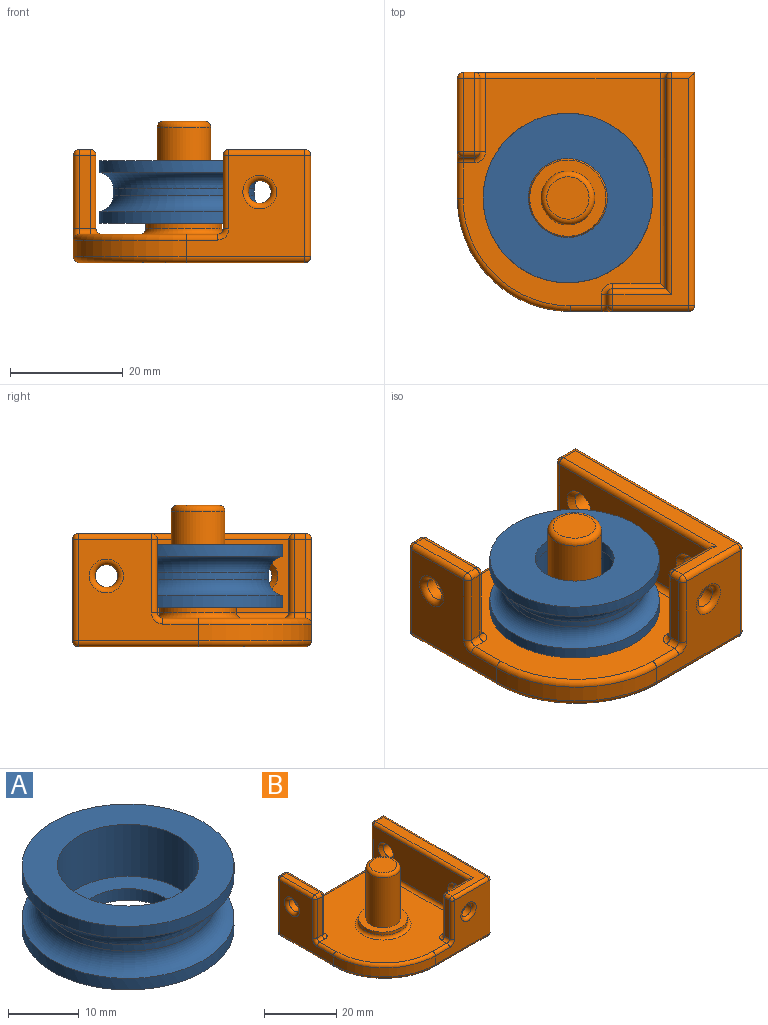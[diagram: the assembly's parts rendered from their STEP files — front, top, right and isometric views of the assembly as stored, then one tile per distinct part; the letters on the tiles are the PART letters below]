
ASSEMBLY  parts=2 mates=1
PART A: 10 faces, bbox 33.6x33.6x11 mm
  f0: plane 20x20mm, normal (0,0,1), area 160.2mm2, adj f1,f4
  f1: cylinder r=7mm len=14mm, axis (0,0,-1), area 88mm2, adj f0,f3
  f2: cylinder r=15mm len=30mm, axis (0,0,-1), area 188.5mm2, adj f3,f8
  f3: plane 30x30mm, normal (0,0,-1), area 552.9mm2, adj f1,f2
  f4: cylinder r=10mm len=20mm, axis (0,0,-1), area 565.5mm2, adj f0,f7
  f5: cylinder r=12.5mm len=25mm, axis (0,0,-1), area 85.1mm2, adj f8,f9
  f6: cylinder r=15mm len=30mm, axis (0,0,-1), area 188.5mm2, adj f7,f9
  f7: plane 30x30mm, normal (0,0,1), area 392.7mm2, adj f4,f6
  f8: torus R=15.5mm, axis (0,0,-1), area 354.3mm2, adj f2,f5
  f9: torus R=15.5mm, axis (0,0,1), area 354.3mm2, adj f5,f6
PART B: 78 faces, bbox 43.6x44x25 mm
  f0: plane 40.3x34.91mm, normal (0,0,1), area 1041.1mm2, adj f35,f36,f43,f48,f49,f59,f60,f63
  f1: plane 41x18mm, normal (0,1,0), area 216.1mm2, adj f5,f24,f34,f42,f46,f47,f48,f53
  f2: plane 21.3x18mm, normal (-1,0,0), area 231.4mm2, adj f3,f45,f55,f65,f68,f70,f71,f73
  f3: cylinder r=20mm len=20mm, axis (0,0,-1), area 94.2mm2, adj f2,f4,f40,f64
  f4: plane 21x18mm, normal (0,-1,0), area 237.7mm2, adj f3,f28,f32,f39,f50,f54,f60,f74
  f5: plane 41.3x18mm, normal (1,0,0), area 718.3mm2, adj f1,f20,f21,f27,f28,f41
  f6: plane 40.3x40mm, normal (0,0,-1), area 1534.6mm2, adj f32,f40,f41,f45,f46
  f7: plane 37.3x13mm, normal (-1,0,0), area 428.4mm2, adj f8,f22,f23,f25,f34,f35
  f8: plane 13x9.38mm, normal (0,1,0), area 93.7mm2, adj f7,f26,f36,f37,f75
  f9: plane 13x2mm, normal (-1,0,0), area 26mm2, adj f37,f38,f49,f50
  f10: plane 40.3x13.47mm, normal (0,0,1), area 145.3mm2, adj f24,f25,f26,f27,f38,f39
  f11: plane 13x12.99mm, normal (1,0,0), area 140.6mm2, adj f47,f57,f58,f59,f72
  f12: plane 13x2mm, normal (0,-1,0), area 26mm2, adj f58,f66,f67,f71
  f13: plane 12.99x2mm, normal (0,0,1), area 26mm2, adj f56,f57,f65,f66
  f14: cylinder r=6.75mm len=13.5mm, axis (0,0,-1), area 42.4mm2, adj f15,f77
  f15: plane 13.5x13.5mm, normal (0,0,1), area 72.3mm2, adj f14,f16
  f16: cylinder r=4.75mm len=17mm, axis (0,0,-1), area 507.4mm2, adj f15,f76
  f17: plane 7.5x7.5mm, normal (0,0,1), area 44.2mm2, adj f76
  f18: cylinder r=2mm len=4mm, axis (0,-1,0), area 25.1mm2, adj f74,f75
  f19: cylinder r=2mm len=4mm, axis (-1,0,0), area 25.1mm2, adj f72,f73
  f20: cylinder r=2mm len=4.09mm, axis (-1,0,0), area 51.4mm2, adj f5,f23
  f21: cylinder r=2mm len=4.09mm, axis (-1,0,0), area 51.4mm2, adj f5,f22
  f22: cone r=2mm half-angle=45deg, axis (-1,0,0), area 22.2mm2, adj f7,f21
  f23: cone r=3mm half-angle=45deg, axis (-1,0,0), area 22.2mm2, adj f7,f20
  f24: cylinder r=1mm len=4.09mm, axis (1,0,0), area 5.9mm2, adj f1,f10,f27,f29
  f25: cylinder r=1mm len=38.3mm, axis (0,1,0), area 59.2mm2, adj f7,f10,f26,f29
  f26: cylinder r=1mm len=10.38mm, axis (1,0,0), area 15.3mm2, adj f8,f10,f25,f30
  f27: cylinder r=1mm len=41.3mm, axis (0,-1,0), area 64.3mm2, adj f5,f10,f24,f31
  f28: cylinder r=1mm len=18mm, axis (0,0,-1), area 28.3mm2, adj f4,f5,f31,f33
  f29: sphere r=1mm, area 1.6mm2, adj f24,f25,f34
  f30: sphere r=1mm, area 1.6mm2, adj f26,f37,f38
  f31: sphere r=1mm, area 1.6mm2, adj f27,f28,f39
  f32: cylinder r=1mm len=21mm, axis (1,0,0), area 33mm2, adj f4,f6,f33,f40
  f33: sphere r=1mm, area 1.6mm2, adj f28,f32,f41
  f34: cylinder r=1mm len=13mm, axis (0,0,1), area 20.4mm2, adj f1,f7,f29,f42
  f35: cylinder r=1mm len=37.3mm, axis (0,1,0), area 58mm2, adj f0,f7,f36,f42
  f36: cylinder r=1mm len=9.38mm, axis (1,0,0), area 14.2mm2, adj f0,f8,f35,f43
  f37: cylinder r=1mm len=13mm, axis (0,0,-1), area 20.4mm2, adj f8,f9,f30,f43
  f38: cylinder r=1mm len=2mm, axis (0,1,0), area 3.1mm2, adj f9,f10,f30,f44
  f39: cylinder r=1mm len=13.47mm, axis (1,0,0), area 21.2mm2, adj f4,f10,f31,f44
  f40: torus R=19mm, axis (0,0,1), area 48.5mm2, adj f3,f6,f32,f45
  f41: cylinder r=1mm len=41.3mm, axis (0,1,0), area 64.3mm2, adj f5,f6,f33,f46
  f42: torus R=2mm, axis (0,1,0), area 3.4mm2, adj f1,f34,f35,f48
  f43: torus R=2mm, axis (0,0,1), area 3.4mm2, adj f0,f36,f37,f49
  f44: sphere r=1mm, area 1.6mm2, adj f38,f39,f50
  f45: cylinder r=1mm len=21.3mm, axis (0,-1,0), area 33.5mm2, adj f2,f6,f40,f51
  f46: cylinder r=1mm len=41mm, axis (-1,0,0), area 63.8mm2, adj f1,f6,f41,f51
  f47: cylinder r=1mm len=13mm, axis (0,0,-1), area 20.4mm2, adj f1,f11,f52,f53
  f48: cylinder r=1mm len=30.91mm, axis (1,0,0), area 48.6mm2, adj f0,f1,f42,f53
  f49: cylinder r=1mm len=2mm, axis (0,1,0), area 3.1mm2, adj f0,f9,f43,f54
  f50: cylinder r=1mm len=13mm, axis (0,0,1), area 20.4mm2, adj f4,f9,f44,f54
  f51: sphere r=1mm, area 1.6mm2, adj f45,f46,f55
  f52: sphere r=1mm, area 1.6mm2, adj f47,f56,f57
  f53: torus R=2mm, axis (0,1,0), area 3.4mm2, adj f1,f47,f48,f59
  f54: torus R=2mm, axis (0,1,0), area 3.4mm2, adj f4,f49,f50,f60
  f55: cylinder r=1mm len=18mm, axis (0,0,1), area 28.3mm2, adj f1,f2,f51,f61
  f56: cylinder r=1mm len=2mm, axis (1,0,0), area 3.1mm2, adj f1,f13,f52,f61
  f57: cylinder r=1mm len=12.99mm, axis (0,-1,0), area 20.4mm2, adj f11,f13,f52,f62
  f58: cylinder r=1mm len=13mm, axis (0,0,1), area 20.4mm2, adj f11,f12,f62,f63
  f59: cylinder r=1mm len=12.99mm, axis (0,-1,0), area 20.4mm2, adj f0,f11,f53,f63
  f60: cylinder r=1mm len=5.53mm, axis (-1,0,0), area 8.7mm2, adj f0,f4,f54,f64
  f61: sphere r=1mm, area 1.6mm2, adj f55,f56,f65
  f62: sphere r=1mm, area 1.6mm2, adj f57,f58,f66
  f63: torus R=2mm, axis (0,0,1), area 3.4mm2, adj f0,f58,f59,f67
  f64: torus R=19mm, axis (0,0,1), area 48.5mm2, adj f0,f3,f60,f68
  f65: cylinder r=1mm len=12.99mm, axis (0,1,0), area 20.4mm2, adj f2,f13,f61,f69
  f66: cylinder r=1mm len=2mm, axis (-1,0,0), area 3.1mm2, adj f12,f13,f62,f69
  f67: cylinder r=1mm len=2mm, axis (-1,0,0), area 3.1mm2, adj f0,f12,f63,f70
  f68: cylinder r=1mm len=6.31mm, axis (0,1,0), area 9.9mm2, adj f0,f2,f64,f70
  f69: sphere r=1mm, area 1.6mm2, adj f65,f66,f71
  f70: torus R=2mm, axis (1,0,0), area 3.4mm2, adj f2,f67,f68,f71
  f71: cylinder r=1mm len=13mm, axis (0,0,-1), area 20.4mm2, adj f2,f12,f69,f70
  f72: torus R=3mm, axis (1,0,0), area 23.3mm2, adj f11,f19
  f73: torus R=3mm, axis (1,0,0), area 23.3mm2, adj f2,f19
  f74: torus R=3mm, axis (0,1,0), area 23.3mm2, adj f4,f18
  f75: torus R=3mm, axis (0,1,0), area 23.3mm2, adj f8,f18
  f76: torus R=3.75mm, axis (0,0,1), area 43.3mm2, adj f16,f17
  f77: torus R=7.75mm, axis (0,0,1), area 70.2mm2, adj f0,f14
PLACE A rot(axis=(-1,0,0),180deg) t=(-11.56,-17.83,21.67)mm
PLACE B t=(-11.56,-17.83,3.67)mm
MATE revolute A.f1 <-> B.f14  axis (0,0,-1) through (-11.56,-17.83,10.67)mm
